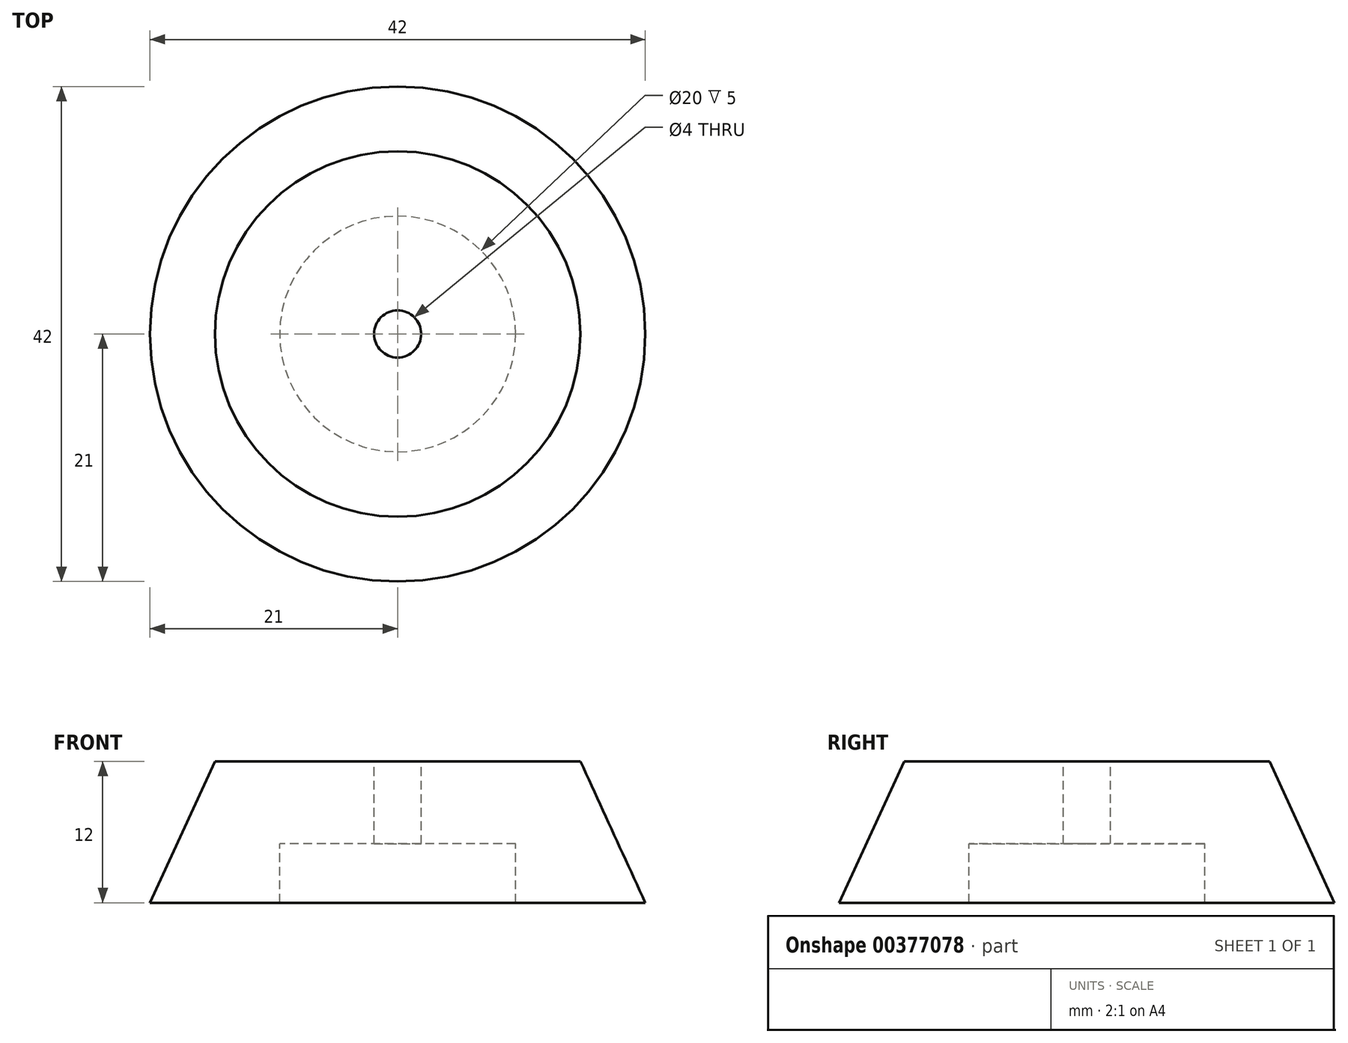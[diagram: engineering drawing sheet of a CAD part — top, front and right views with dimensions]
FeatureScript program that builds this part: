
annotation { "Feature Type Name" : "Feature", "Feature Type Description" : "" }
export const myFeature = defineFeature(function(context is Context, id is Id, definition is map)
    precondition{}
    {
        {
            var Q0;
            Q0=qCreatedBy(makeId("Front.planeOp"),FACE);
            var sketch = newSketch(context, id + "F0", { "sketchPlane" : qUnion([Q0])});
            skLineSegment(sketch, "E0", {"start": v(-21, 0) * mm, "end": v(-15.5, 12) * mm});
            skLineSegment(sketch, "E1", {"start": v(-15.5, 12) * mm, "end": v(0, 12) * mm});
            skLineSegment(sketch, "E2", {"start": v(-10, 0) * mm, "end": v(-10, 5) * mm});
            skLineSegment(sketch, "E3", {"start": v(-10, 5) * mm, "end": v(0, 5) * mm});
            skLineSegment(sketch, "E4", {"start": v(-21, 0) * mm, "end": v(-10, 0) * mm});
            skLineSegment(sketch, "E5", {"start": v(0, 12) * mm, "end": v(0, 5) * mm});
            skSolve(sketch);
        }
        {
            var Q0;
            Q0=makeQuery(id+"F0.imprint","IMPRINT",FACE,{"disambiguationData":[TD([[makeQuery(id+"F0.imprint","IMPRINT",EDGE,{"derivedFrom":sQuery(id+"F0.wireOp",EDGE,"E0")}),-1.0]])]});
            var Q1;
            Q1=sQuery(id+"F0.wireOp",EDGE,"E5");
            revolve(context, id + "F1", {"entities" : qUnion([Q0]), "axis" : qUnion([Q1]), "revolveType" : RevolveType.FULL});
        }
        {
            var Q0;
            Q0=makeQuery(id+"F1.opRevolve","SWEPT_FACE",FACE,{"disambiguationData":[OSD([sQuery(id+"F0.wireOp",EDGE,"E1")])]});
            var sketch = newSketch(context, id + "F2", { "sketchPlane" : qUnion([Q0])});
            skCircle(sketch, "E6.0.0", {"center": v(0, 0) * mm, "radius": 15.5 * mm});
            skSolve(sketch);
        }
        {
            var Q0;
            Q0=sQuery(id+"F2.wireOp",VERTEX,"E6.0.0.center");
            var Q1;
            Q1=makeQuery(id+"F1.opRevolve","SWEPT_BODY",BODY,{"disambiguationData":[OSD([sQuery(id+"F0.wireOp",EDGE,"E0"),sQuery(id+"F0.wireOp",EDGE,"E1"),sQuery(id+"F0.wireOp",EDGE,"E2"),sQuery(id+"F0.wireOp",EDGE,"E3"),sQuery(id+"F0.wireOp",EDGE,"E4"),sQuery(id+"F0.wireOp",EDGE,"E5")])]});
            hole(context, id + "F3", {"style" : HoleStyle.SIMPLE, "endStyle" : HoleEndStyle.THROUGH, "holeDiameter" : 4 * mm, "isTappedThrough" : true, "tappedDepth" : 12 * mm, "tapClearance" : 3, "locations" : qUnion([Q0]), "scope" : qUnion([Q1])});
        }
    });
